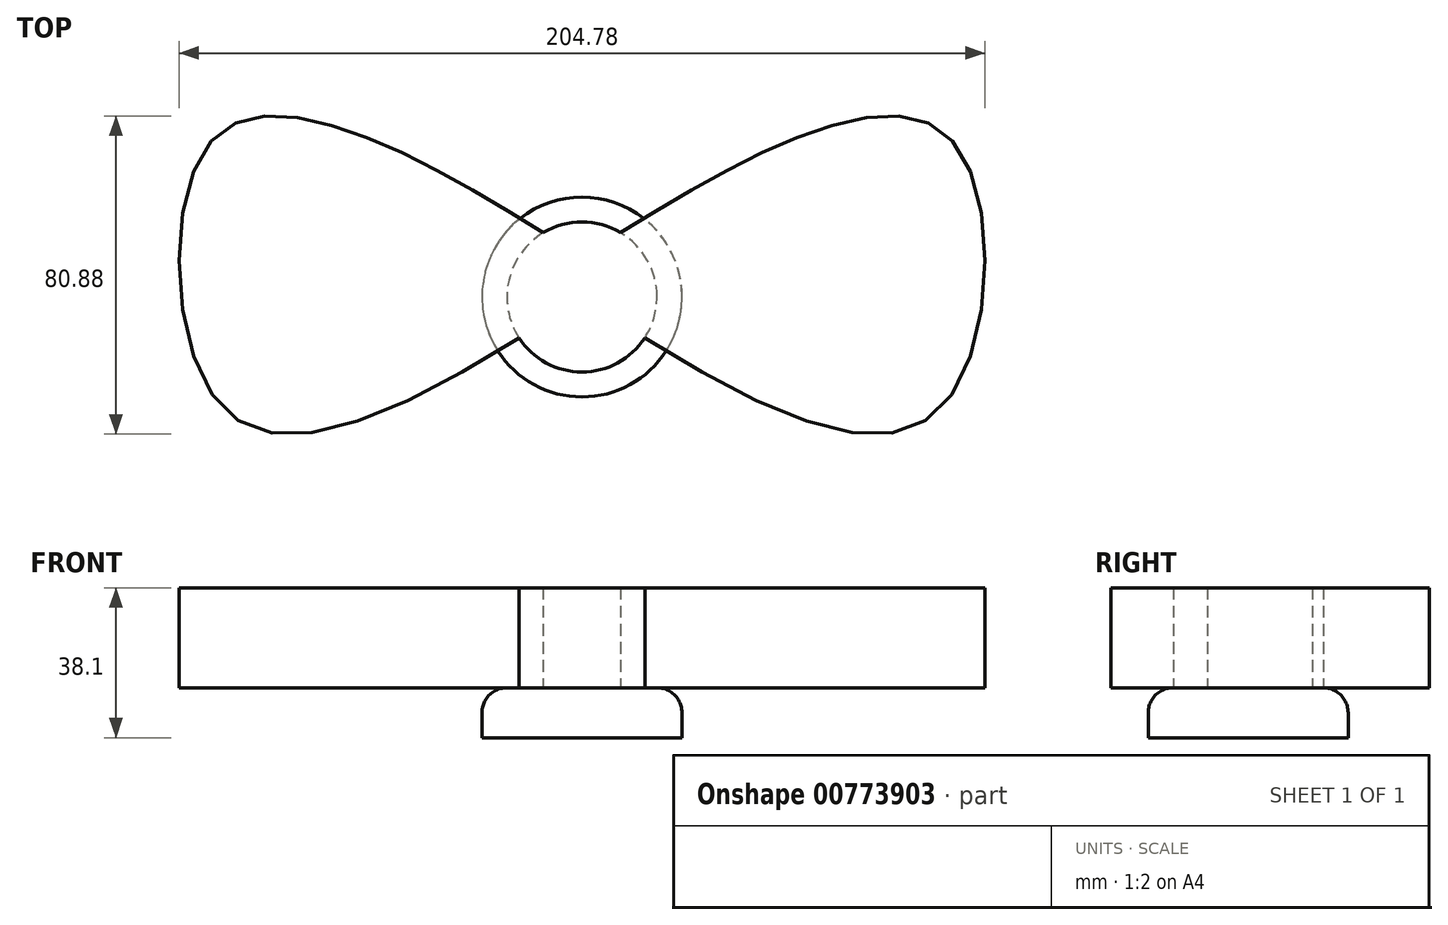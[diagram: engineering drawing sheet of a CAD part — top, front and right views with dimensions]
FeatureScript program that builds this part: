
annotation { "Feature Type Name" : "Feature", "Feature Type Description" : "" }
export const myFeature = defineFeature(function(context is Context, id is Id, definition is map)
    precondition{}
    {
        {
            var Q0;
            Q0=qCreatedBy(makeId("Top.planeOp"),FACE);
            var sketch = newSketch(context, id + "F0", { "sketchPlane" : qUnion([Q0])});
            skCircle(sketch, "E0", {"center": v(0, 0) * mm, "radius": 25.4 * mm});
            skSolve(sketch);
        }
        {
            var Q0;
            Q0 = qSketchRegion(id + "F0", true);
            extrude(context, id + "F1", {"entities" : qUnion([Q0]), "depth" : 12.7 * mm, "offsetDistance" : 25.4 * mm});
        }
        {
            var Q0;
            Q0=makeQuery(id+"F1.opExtrude","CAP_EDGE",EDGE,{"disambiguationData":[OSD([sQuery(id+"F0.wireOp",EDGE,"E0")])],"isStart":false});
            fillet(context, id + "F2", {"entities" : qUnion([Q0]), "radius" : 6.35 * mm, "tangentPropagation" : true, "allowEdgeOverflow" : false});
        }
        {
            var Q0;
            Q0=makeQuery(id+"F1.opExtrude","CAP_FACE",FACE,{"disambiguationData":[OSD([sQuery(id+"F0.wireOp",EDGE,"E0")])],"isStart":false});
            var sketch = newSketch(context, id + "F3", { "sketchPlane" : qUnion([Q0])});
            skCircle(sketch, "E1", {"center": v(0, 0) * mm, "radius": 19.05 * mm});
            skFitSpline(sketch, "E2", {"points": [v(-9.83, 16.32) * mm, v(-62.6, 43.29) * mm, v(-95.96, 37.27) * mm, v(-90.13, -29.25) * mm, v(0, 0) * mm], "startDerivative": vector(-216.6, 132.42) * mm, "endDerivative": vector(366.28, 244.48) * mm});
            skLineSegment(sketch, "E3", {"start": v(0, 39.1) * mm, "end": v(0, -50.94) * mm, "construction": true});
            skFitSpline(sketch, "E4.MirrorCS", {"points": [v(9.83, 16.32) * mm, v(62.6, 43.29) * mm, v(95.96, 37.27) * mm, v(90.13, -29.25) * mm, v(0, 0) * mm], "startDerivative": vector(216.6, 132.42) * mm, "endDerivative": vector(-366.28, 244.48) * mm});
            skSolve(sketch);
        }
        {
            var Q0;
            Q0 = qSketchRegion(id + "F3", true);
            extrude(context, id + "F4", {"entities" : qUnion([Q0]), "operationType" : NewBodyOperationType.ADD, "depth" : 25.4 * mm, "offsetDistance" : 25.4 * mm});
        }
    });
